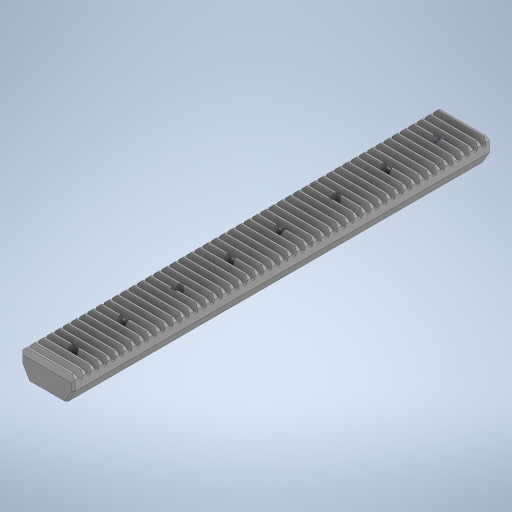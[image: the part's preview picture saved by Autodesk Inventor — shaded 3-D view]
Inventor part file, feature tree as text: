
AUTODESK INVENTOR PART (.ipt)
format: ipt  version: 2023.1 (Build 271208000, 208)  size: 1,534,464 bytes
history: native  units: mm
features: other x1, chamfer x1
ambient origin geometry x8: Origin, YZ Plane, XZ Plane, XY Plane, X Axis, Y Axis, Z Axis, Center Point
bodies: Solid1 (feature_tree)
feature tree (2):
  other  "39300B_TXM-Linear Slide Rail.STEP"
  chamfer  "Chamfer1"  [1 undecoded]
note: 1 required parameter value undecoded (feature->parameter linkage not recoverable at this tier; creation-order binding heuristic only, values carry confidence <= 0.55)
